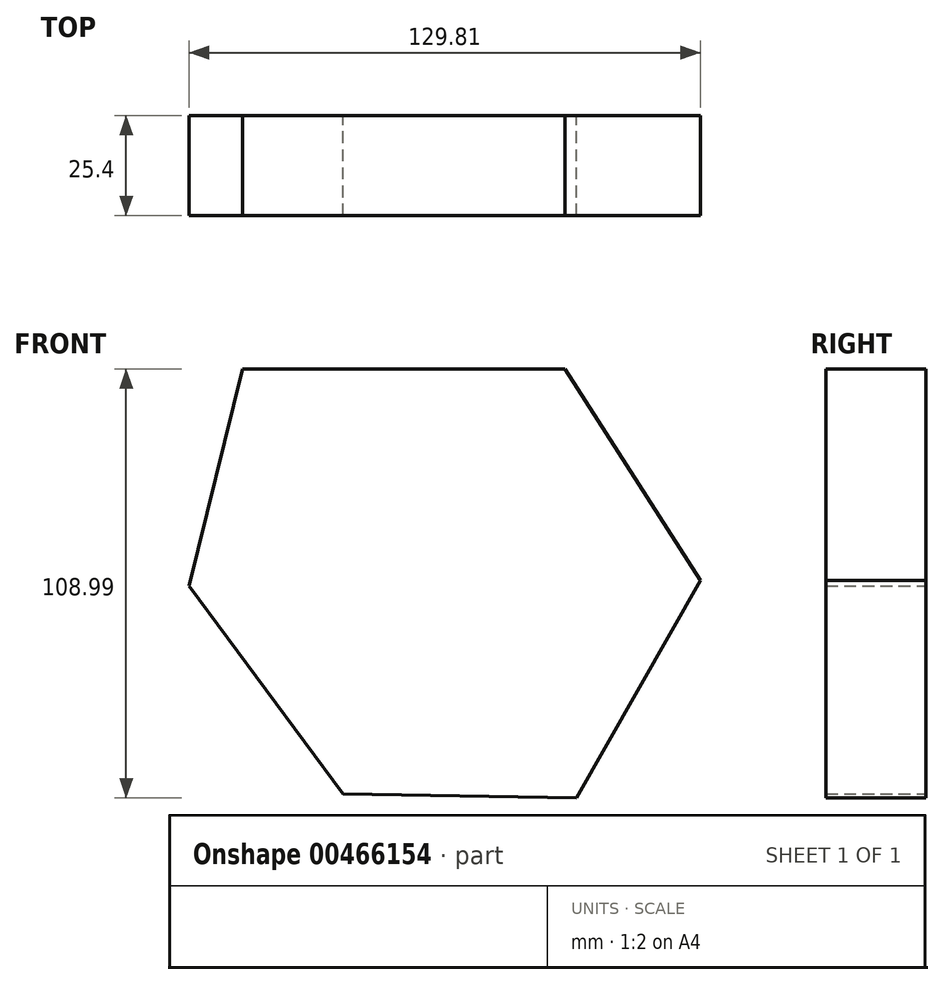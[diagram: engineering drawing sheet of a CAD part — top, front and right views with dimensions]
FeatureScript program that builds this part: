
annotation { "Feature Type Name" : "Feature", "Feature Type Description" : "" }
export const myFeature = defineFeature(function(context is Context, id is Id, definition is map)
    precondition{}
    {
        {
            var Q0;
            Q0=qCreatedBy(makeId("Front.planeOp"),FACE);
            var sketch = newSketch(context, id + "F0", { "sketchPlane" : qUnion([Q0])});
            skLineSegment(sketch, "E0", {"start": v(33.14, 55.15) * mm, "end": v(-48.72, 55.15) * mm});
            skLineSegment(sketch, "E1", {"start": v(-48.72, 55.15) * mm, "end": v(-62.26, 0) * mm});
            skLineSegment(sketch, "E2", {"start": v(-62.26, 0) * mm, "end": v(-23.25, -52.74) * mm});
            skLineSegment(sketch, "E3", {"start": v(-23.25, -52.74) * mm, "end": v(36.06, -53.84) * mm});
            skLineSegment(sketch, "E4", {"start": v(36.06, -53.84) * mm, "end": v(67.55, 1.48) * mm});
            skLineSegment(sketch, "E5", {"start": v(67.55, 1.48) * mm, "end": v(33.14, 55.15) * mm});
            skSolve(sketch);
        }
        {
            var Q0;
            Q0=makeQuery(id+"F0.imprint","IMPRINT",FACE,{"disambiguationData":[TD([[makeQuery(id+"F0.imprint","IMPRINT",EDGE,{"derivedFrom":sQuery(id+"F0.wireOp",EDGE,"E0")}),1.0]])]});
            extrude(context, id + "F1", {"entities" : qUnion([Q0]), "depth" : 25.4 * mm});
        }
    });
